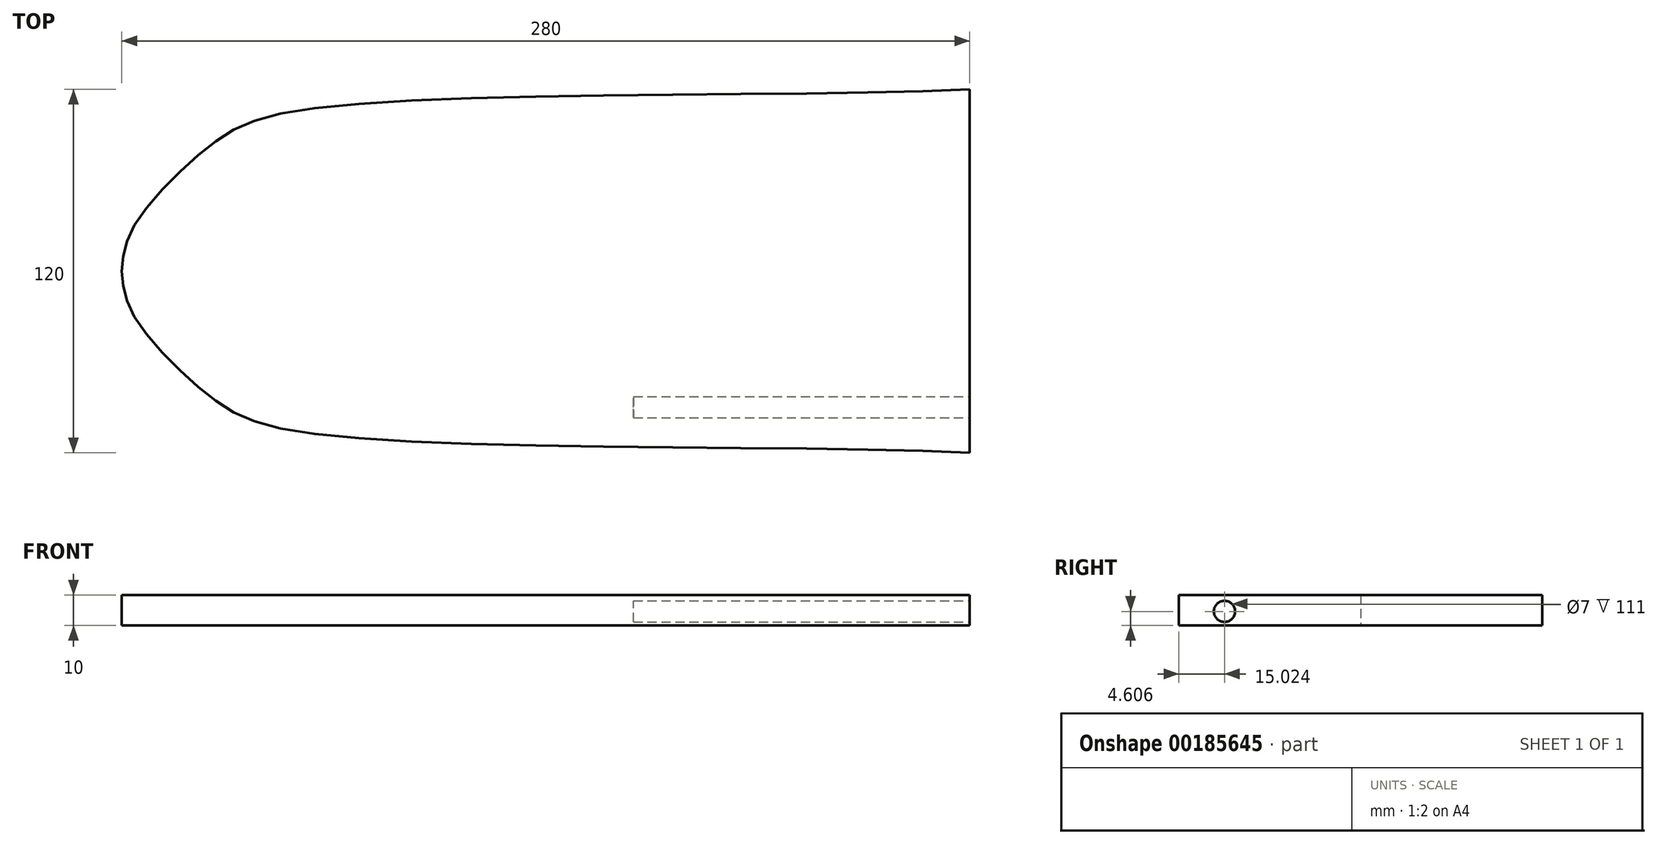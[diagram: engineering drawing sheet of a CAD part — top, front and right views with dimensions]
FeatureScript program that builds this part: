
annotation { "Feature Type Name" : "Feature", "Feature Type Description" : "" }
export const myFeature = defineFeature(function(context is Context, id is Id, definition is map)
    precondition{}
    {
        {
            var Q0;
            Q0=qCreatedBy(makeId("Top.planeOp"),FACE);
            var sketch = newSketch(context, id + "F0", { "sketchPlane" : qUnion([Q0])});
            skLineSegment(sketch, "E0", {"start": v(0, 0) * mm, "end": v(-280, 0) * mm});
            skLineSegment(sketch, "E1", {"start": v(0, 0) * mm, "end": v(0, -60) * mm});
            skFitSpline(sketch, "E2", {"points": [v(-280, 0) * mm, v(-276.1, -14.72) * mm, v(-253.03, -39.76) * mm, v(-216.76, -53.76) * mm, v(0, -60) * mm], "startDerivative": vector(6.95, -116.06) * mm, "endDerivative": vector(320.34, -16.92) * mm});
            skFitSpline(sketch, "E3.MirrorCS", {"points": [v(-280, 0) * mm, v(-276.1, 14.72) * mm, v(-253.03, 39.76) * mm, v(-216.76, 53.76) * mm, v(0, 60) * mm], "startDerivative": vector(6.95, 116.06) * mm, "endDerivative": vector(320.34, 16.92) * mm});
            skLineSegment(sketch, "E4.MirrorCS", {"start": v(0, 0) * mm, "end": v(0, 60) * mm});
            skSolve(sketch);
        }
        {
            var Q0;
            Q0=makeQuery(id+"F0.imprint","IMPRINT",FACE,{"disambiguationData":[TD([[makeQuery(id+"F0.imprint","IMPRINT",EDGE,{"derivedFrom":sQuery(id+"F0.wireOp",EDGE,"E0")}),-1.0]])]});
            var Q1;
            Q1=makeQuery(id+"F0.imprint","IMPRINT",FACE,{"disambiguationData":[TD([[makeQuery(id+"F0.imprint","IMPRINT",EDGE,{"derivedFrom":sQuery(id+"F0.wireOp",EDGE,"E0")}),1.0]])]});
            extrude(context, id + "F1", {"entities" : qUnion([Q0, Q1]), "depth" : 10 * mm});
        }
        {
            var Q0;
            Q0=qCreatedBy(makeId("Right.planeOp"),FACE);
            var sketch = newSketch(context, id + "F2", { "sketchPlane" : qUnion([Q0])});
            skCircle(sketch, "E5", {"center": v(-44.98, 4.6) * mm, "radius": 3.5 * mm});
            skCircle(sketch, "E6.MirrorC", {"center": v(44.98, 4.6) * mm, "radius": 3.5 * mm});
            skSolve(sketch);
        }
        {
            var Q0;
            Q0=makeQuery(id+"F2.imprint","IMPRINT",FACE,{"disambiguationData":[TD([[makeQuery(id+"F2.imprint","IMPRINT",EDGE,{"derivedFrom":sQuery(id+"F2.wireOp",EDGE,"E5")}),1.0]])]});
            var Q1;
            Q1=makeQuery(id+"F2.imprint","IMPRINT",FACE,{"disambiguationData":[TD([[makeQuery(id+"F2.imprint","IMPRINT",EDGE,{"derivedFrom":sQuery(id+"F2.wireOp",EDGE,"E6.MirrorC")}),-1.0]])]});
            extrude(context, id + "F3", {"entities" : qUnion([Q0, Q1]), "operationType" : NewBodyOperationType.REMOVE, "oppositeDirection" : true, "depth" : 111 * mm});
        }
    });
